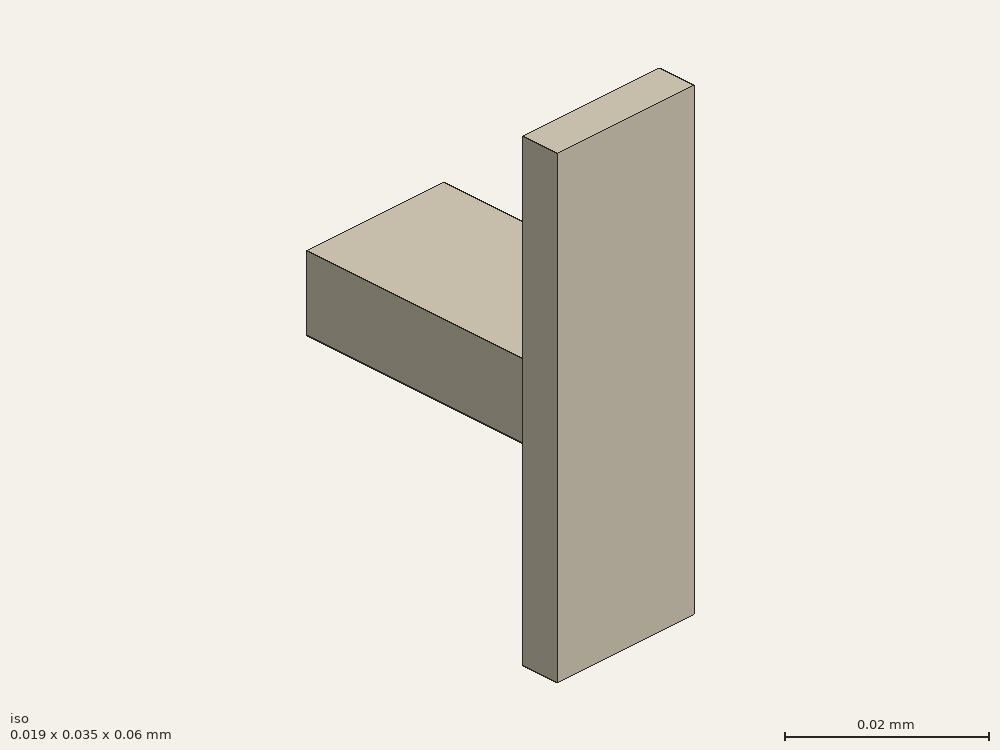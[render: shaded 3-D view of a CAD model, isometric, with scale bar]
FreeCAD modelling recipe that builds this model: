
FCSTD DOCUMENT  (FreeCAD 0.21R33694 (Git))
Label: T-Junction
License: All rights reserved
LicenseURL: http://en.wikipedia.org/wiki/All_rights_reserved
objects: Part::Part2DObjectPython×8, App::FeaturePython×6, Part::Extrusion×2, Part::MultiFuse×1, Part::FeaturePython×1
note: 12 computed .brp shape members not serialized (recipe doc carries the construction recipe); baked Part::Feature solids carry a one-line shape summary decoded from their .brp

FEATURE [Part::Part2DObjectPython] Rectangle  # Draft 2D object (typed FeaturePython)
  Area = 181.356
  ChamferSize = 0
  Columns = 1
  FilletRadius = 0
  Height = 9.52
  Length = 19.05
  MakeFace = true
  Placement = pos=(-9.525,0,0) rot=(0,0,1;0rad)
  Rows = 1
FEATURE [Part::Part2DObjectPython] Rectangle001  # Draft 2D object (typed FeaturePython)
  Area = 90.678
  ChamferSize = 0
  Columns = 1
  FilletRadius = 0
  Height = 4.76
  Length = 19.05
  MakeFace = true
  Placement = pos=(-9.525,0,0) rot=(0,0,1;0rad)
  Rows = 1
FEATURE [Part::Extrusion] Extrude
  Base = -> Rectangle
  Dir = (0,0,1)
  DirMode = 2
  FaceMakerClass = Part::FaceMakerBullseye
  LengthFwd = 30
  LengthRev = 0
  Placement = pos=(0,34.76,55.24) rot=(1,0,0;1.5708rad)
  Solid = false
  Symmetric = false
FEATURE [Part::Extrusion] Extrude001
  Base = -> Rectangle001
  Dir = (0,0,1)
  DirMode = 2
  FaceMakerClass = Part::FaceMakerBullseye
  LengthFwd = 60
  LengthRev = 0
  Placement = pos=(0,0,30) rot=(0,0,1;0rad)
  Solid = false
  Symmetric = false
FEATURE [Part::MultiFuse] Fusion
  Shapes = -> [Extrude,Extrude001]
FEATURE [Part::FeaturePython] Clone  label="scaled"  # Draft clone (typed FeaturePython)
  AttacherType = Attacher::AttachEngine3D
  Fuse = false
  Objects = -> [Fusion]
  Scale = (0.001,0.001,0.001)
FEATURE [Part::Part2DObjectPython] Rectangle002  label="_P1"  # Draft 2D object (typed FeaturePython)
  Area = 0.000181356
  ChamferSize = 0
  Columns = 1
  FilletRadius = 0
  Height = 0.00952
  Length = 0.01905
  MakeFace = true
  Placement = pos=(0.009525,0.03476,0.05524) rot=(0,0.707107,0.707107;3.14159rad)
  Rows = 1
FEATURE [Part::Part2DObjectPython] Line  label="_PV1"  # Draft 2D object (typed FeaturePython)
  Area = 0
  ChamferSize = 0
  Closed = false
  End = (0,0.03476,0.06476)
  FilletRadius = 0
  Length = 0.00952
  MakeFace = true
  Placement = pos=(0,0.03476,0.05524) rot=(0,0.707107,0.707107;3.14159rad)
  Points = (2) [(0,0,0),(0,0.00952,0)]
  Start = (0,0.03476,0.05524)
  Subdivisions = 0
FEATURE [Part::Part2DObjectPython] Rectangle003  label="_P2"  # Draft 2D object (typed FeaturePython)
  Area = 9.0678e-05
  ChamferSize = 0
  Columns = 1
  FilletRadius = 0
  Height = 0.00476
  Length = 0.01905
  MakeFace = true
  Placement = pos=(-0.009525,0,0.09) rot=(0,0,1;0rad)
  Rows = 1
FEATURE [Part::Part2DObjectPython] Line001  label="_PV2"  # Draft 2D object (typed FeaturePython)
  Area = 0
  ChamferSize = 0
  Closed = false
  End = (0,0.00476,0.09)
  FilletRadius = 0
  Length = 0.00476
  MakeFace = true
  Placement = pos=(0,0,0.09) rot=(0,0,1;0rad)
  Points = (2) [(0,0,0),(0,0.00476,-3.3723e-15)]
  Start = (0,0,0.09)
  Subdivisions = 0
FEATURE [Part::Part2DObjectPython] Rectangle004  label="_P3"  # Draft 2D object (typed FeaturePython)
  Area = 9.0678e-05
  ChamferSize = 0
  Columns = 1
  FilletRadius = 0
  Height = 0.01905
  Length = 0.00476
  MakeFace = true
  Placement = pos=(-0.009525,0,0.03) rot=(0.707107,0.707107,0;3.14159rad)
  Rows = 1
FEATURE [Part::Part2DObjectPython] Line002  label="_PV3"  # Draft 2D object (typed FeaturePython)
  Area = 0
  ChamferSize = 0
  Closed = false
  End = (0,0.00476,0.03)
  FilletRadius = 0
  Length = 0.00476
  MakeFace = true
  Placement = pos=(0,0,0.03) rot=(0.707107,0.707107,0;3.14159rad)
  Points = (2) [(0,0,0),(0.00476,-1.05693e-18,0)]
  Start = (0,0,0.03)
  Subdivisions = 0
FEATURE [App::FeaturePython] Text  label="_S1(PV){1}"  # WARN: FeaturePython — macro-defined, semantics opaque (R4)
  Placement = pos=(0.00560265,-0.0253095,0.03) rot=(0.707107,0.707107,0;3.14159rad)
  Text = .
FEATURE [App::FeaturePython] Text001  label="_S2(PV){2}"  # WARN: FeaturePython — macro-defined, semantics opaque (R4)
  Placement = pos=(0.00560265,-0.0253095,0.03) rot=(0.707107,0.707107,0;3.14159rad)
  Text = .
FEATURE [App::FeaturePython] Text002  label="_S3(PV){3}"  # WARN: FeaturePython — macro-defined, semantics opaque (R4)
  Placement = pos=(0.00560265,-0.0253095,0.03) rot=(0.707107,0.707107,0;3.14159rad)
  Text = .
FEATURE [App::FeaturePython] Text004  label="_M1(1,voltage){V1}"  # WARN: FeaturePython — macro-defined, semantics opaque (R4)
  Placement = pos=(0.00560265,-0.0253095,0.03) rot=(0.707107,0.707107,0;3.14159rad)
  Text = .
FEATURE [App::FeaturePython] Text005  label="_M2(2,voltage){V2}"  # WARN: FeaturePython — macro-defined, semantics opaque (R4)
  Placement = pos=(0.00560265,-0.0253095,0.03) rot=(0.707107,0.707107,0;3.14159rad)
  Text = .
FEATURE [App::FeaturePython] Text006  label="_M3(3,voltage){V3}"  # WARN: FeaturePython — macro-defined, semantics opaque (R4)
  Placement = pos=(0.00560265,-0.0253095,0.03) rot=(0.707107,0.707107,0;3.14159rad)
  Text = .
